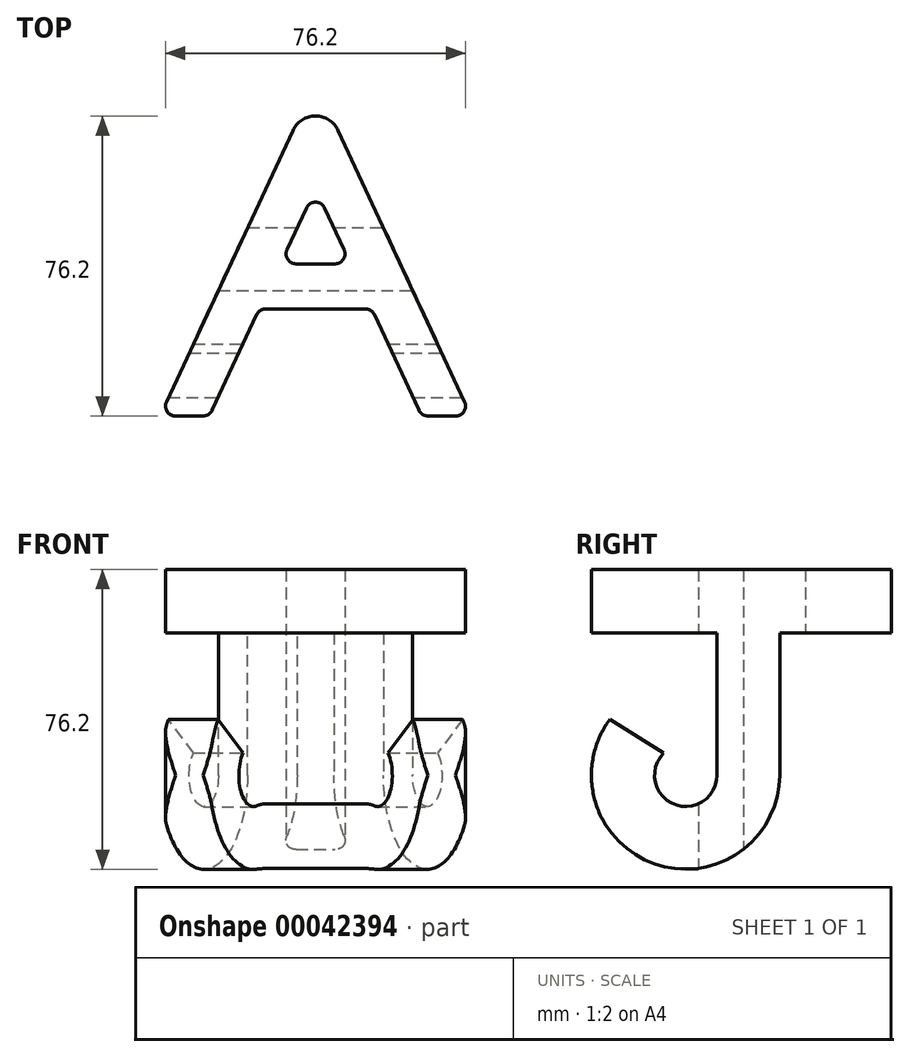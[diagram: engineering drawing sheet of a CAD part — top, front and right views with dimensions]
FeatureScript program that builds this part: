
annotation { "Feature Type Name" : "Feature", "Feature Type Description" : "" }
export const myFeature = defineFeature(function(context is Context, id is Id, definition is map)
    precondition{}
    {
        {
            var Q0;
            Q0=qCreatedBy(makeId("Top.planeOp"),FACE);
            var sketch = newSketch(context, id + "F0", { "sketchPlane" : qUnion([Q0])});
            skLineSegment(sketch, "E0.rect.bottom", {"start": v(38.1, -38.1) * mm, "end": v(-38.1, -38.1) * mm, "construction": true});
            skLineSegment(sketch, "E0.rect.top", {"start": v(38.1, 38.1) * mm, "end": v(-38.1, 38.1) * mm, "construction": true});
            skLineSegment(sketch, "E0.rect.left", {"start": v(38.1, -38.1) * mm, "end": v(38.1, 38.1) * mm, "construction": true});
            skLineSegment(sketch, "E0.rect.right", {"start": v(-38.1, -38.1) * mm, "end": v(-38.1, 38.1) * mm, "construction": true});
            skPoint(sketch, "E0.rect.middle", {"position": v(0, 0) * mm});
            skLineSegment(sketch, "E1", {"start": v(5.76, 34.43) * mm, "end": v(37.86, -34.49) * mm});
            skLineSegment(sketch, "E2", {"start": v(35.56, -38.1) * mm, "end": v(28.55, -38.1) * mm});
            skLineSegment(sketch, "E3", {"start": v(26.25, -36.63) * mm, "end": v(14.94, -12.34) * mm});
            skLineSegment(sketch, "E4", {"start": v(12.63, -10.87) * mm, "end": v(-12.63, -10.87) * mm});
            skLineSegment(sketch, "E5", {"start": v(-14.94, -12.34) * mm, "end": v(-26.25, -36.63) * mm});
            skLineSegment(sketch, "E6", {"start": v(-28.55, -38.1) * mm, "end": v(-35.56, -38.1) * mm});
            skLineSegment(sketch, "E7", {"start": v(-37.86, -34.49) * mm, "end": v(-5.76, 34.43) * mm});
            skLineSegment(sketch, "E8", {"start": v(2.3, 14.78) * mm, "end": v(7.24, 4.17) * mm});
            skLineSegment(sketch, "E9", {"start": v(4.94, 0.56) * mm, "end": v(-4.94, 0.56) * mm});
            skLineSegment(sketch, "E10", {"start": v(-7.24, 4.17) * mm, "end": v(-2.3, 14.78) * mm});
            skLineSegment(sketch, "E11", {"start": v(-26.94, -38.1) * mm, "end": v(26.94, -38.1) * mm, "construction": true});
            skPoint(sketch, "E12", {"position": v(0, -38.1) * mm});
            skLineSegment(sketch, "E13", {"start": v(-1.57, 0.56) * mm, "end": v(-1.57, -10.87) * mm, "construction": true});
            skLineSegment(sketch, "E14", {"start": v(-8.93, 0.56) * mm, "end": v(-19.29, 5.38) * mm, "construction": true});
            skPoint(sketch, "E15.visualSharp", {"position": v(0, 46.79) * mm});
            skArc(sketch, "E15.filletArc", {"start": v(5.76, 34.43) * mm, "mid": v(0, 38.1) * mm, "end": v(-5.76, 34.43) * mm});
            skPoint(sketch, "E16.visualSharp", {"position": v(0, 19.72) * mm});
            skArc(sketch, "E16.filletArc", {"start": v(2.3, 14.78) * mm, "mid": v(0, 16.25) * mm, "end": v(-2.3, 14.78) * mm});
            skPoint(sketch, "E17.visualSharp", {"position": v(8.93, 0.56) * mm});
            skArc(sketch, "E17.filletArc", {"start": v(4.94, 0.56) * mm, "mid": v(7.08, 1.73) * mm, "end": v(7.24, 4.17) * mm});
            skPoint(sketch, "E18.visualSharp", {"position": v(-8.93, 0.56) * mm});
            skArc(sketch, "E18.filletArc", {"start": v(-7.24, 4.17) * mm, "mid": v(-7.08, 1.73) * mm, "end": v(-4.94, 0.56) * mm});
            skPoint(sketch, "E19.visualSharp", {"position": v(-14.25, -10.87) * mm});
            skArc(sketch, "E19.filletArc", {"start": v(-12.63, -10.87) * mm, "mid": v(-14, -11.27) * mm, "end": v(-14.94, -12.34) * mm});
            skPoint(sketch, "E20.visualSharp", {"position": v(14.25, -10.87) * mm});
            skArc(sketch, "E20.filletArc", {"start": v(14.94, -12.34) * mm, "mid": v(14, -11.27) * mm, "end": v(12.63, -10.87) * mm});
            skPoint(sketch, "E21.visualSharp", {"position": v(-39.55, -38.1) * mm});
            skArc(sketch, "E21.filletArc", {"start": v(-37.86, -34.49) * mm, "mid": v(-37.7, -36.93) * mm, "end": v(-35.56, -38.1) * mm});
            skPoint(sketch, "E22.visualSharp", {"position": v(-26.94, -38.1) * mm});
            skArc(sketch, "E22.filletArc", {"start": v(-28.55, -38.1) * mm, "mid": v(-27.19, -37.7) * mm, "end": v(-26.25, -36.63) * mm});
            skPoint(sketch, "E23.visualSharp", {"position": v(26.94, -38.1) * mm});
            skArc(sketch, "E23.filletArc", {"start": v(26.25, -36.63) * mm, "mid": v(27.19, -37.7) * mm, "end": v(28.55, -38.1) * mm});
            skPoint(sketch, "E24.visualSharp", {"position": v(39.55, -38.1) * mm});
            skArc(sketch, "E24.filletArc", {"start": v(35.56, -38.1) * mm, "mid": v(37.7, -36.93) * mm, "end": v(37.86, -34.49) * mm});
            skPoint(sketch, "E25", {"position": v(0, 38.1) * mm});
            skLineSegment(sketch, "E26", {"start": v(16.02, -14.67) * mm, "end": v(26.38, -9.85) * mm, "construction": true});
            skSolve(sketch);
        }
        {
            var Q0;
            Q0=makeQuery(id+"F0.imprint","IMPRINT",FACE,{"disambiguationData":[TD([[makeQuery(id+"F0.imprint","IMPRINT",EDGE,{"derivedFrom":sQuery(id+"F0.wireOp",EDGE,"E1")}),-1.0]])]});
            extrude(context, id + "F1", {"entities" : qUnion([Q0]), "depth" : 76.2 * mm, "symmetric" : true});
        }
        {
            var Q0;
            Q0=qCreatedBy(makeId("Right.planeOp"),FACE);
            var sketch = newSketch(context, id + "F2", { "sketchPlane" : qUnion([Q0])});
            skLineSegment(sketch, "E27.rect.bottom", {"start": v(-38.1, -38.1) * mm, "end": v(38.1, -38.1) * mm, "construction": true});
            skLineSegment(sketch, "E27.rect.top", {"start": v(-38.1, 38.1) * mm, "end": v(38.1, 38.1) * mm, "construction": true});
            skLineSegment(sketch, "E27.rect.left", {"start": v(-38.1, -38.1) * mm, "end": v(-38.1, 38.1) * mm, "construction": true});
            skLineSegment(sketch, "E27.rect.right", {"start": v(38.1, -38.1) * mm, "end": v(38.1, 38.1) * mm, "construction": true});
            skPoint(sketch, "E27.rect.middle", {"position": v(0, 0) * mm});
            skLineSegment(sketch, "E28", {"start": v(38.1, 38.1) * mm, "end": v(38.1, -38.1) * mm});
            skLineSegment(sketch, "E29", {"start": v(38.1, -38.1) * mm, "end": v(-38.1, -38.1) * mm});
            skLineSegment(sketch, "E30", {"start": v(-38.1, -38.1) * mm, "end": v(-38.1, -14.86) * mm});
            skLineSegment(sketch, "E31", {"start": v(-38.1, -14.86) * mm, "end": v(14.86, -14.86) * mm});
            skLineSegment(sketch, "E32", {"start": v(14.86, -14.86) * mm, "end": v(14.86, 38.1) * mm});
            skLineSegment(sketch, "E33", {"start": v(14.86, 38.1) * mm, "end": v(38.1, 38.1) * mm});
            skSolve(sketch);
        }
        {
            var Q0;
            Q0=qCreatedBy(makeId("Right.planeOp"),FACE);
            var sketch = newSketch(context, id + "F3", { "sketchPlane" : qUnion([Q0])});
            skLineSegment(sketch, "E34.rect.bottom", {"start": v(38.1, -38.1) * mm, "end": v(-38.1, -38.1) * mm, "construction": true});
            skLineSegment(sketch, "E34.rect.top", {"start": v(38.1, 38.1) * mm, "end": v(-38.1, 38.1) * mm, "construction": true});
            skLineSegment(sketch, "E34.rect.left", {"start": v(38.1, -38.1) * mm, "end": v(38.1, 38.1) * mm, "construction": true});
            skLineSegment(sketch, "E34.rect.right", {"start": v(-38.1, -38.1) * mm, "end": v(-38.1, 38.1) * mm, "construction": true});
            skPoint(sketch, "E34.rect.middle", {"position": v(0, 0) * mm});
            skLineSegment(sketch, "E35", {"start": v(-38.1, 38.1) * mm, "end": v(38.1, 38.1) * mm});
            skLineSegment(sketch, "E36", {"start": v(38.1, 38.1) * mm, "end": v(38.1, 22.02) * mm});
            skLineSegment(sketch, "E37", {"start": v(38.1, 22.02) * mm, "end": v(9.77, 22.02) * mm});
            skLineSegment(sketch, "E38", {"start": v(9.77, 22.02) * mm, "end": v(9.77, -14.16) * mm});
            skLineSegment(sketch, "E39", {"start": v(-38.1, 38.1) * mm, "end": v(-38.1, 22.02) * mm});
            skLineSegment(sketch, "E40", {"start": v(-38.1, 22.02) * mm, "end": v(-6.18, 22.02) * mm});
            skLineSegment(sketch, "E41", {"start": v(-6.18, 22.02) * mm, "end": v(-6.18, -14.16) * mm});
            skArc(sketch, "E42", {"start": v(9.77, -14.16) * mm, "mid": v(-21.62, -36.91) * mm, "end": v(-33.46, 0) * mm});
            skArc(sketch, "E43", {"start": v(-6.18, -14.16) * mm, "mid": v(-17.22, -21.55) * mm, "end": v(-19.82, -8.52) * mm});
            skLineSegment(sketch, "E44", {"start": v(-33.46, 0) * mm, "end": v(-19.82, -8.52) * mm});
            skSolve(sketch);
        }
        {
            var Q0;
            Q0 = qSketchRegion(id + "F3", true);
            extrude(context, id + "F4", {"entities" : qUnion([Q0]), "operationType" : NewBodyOperationType.INTERSECT, "oppositeDirection" : true, "depth" : 127 * mm, "symmetric" : true});
        }
    });
